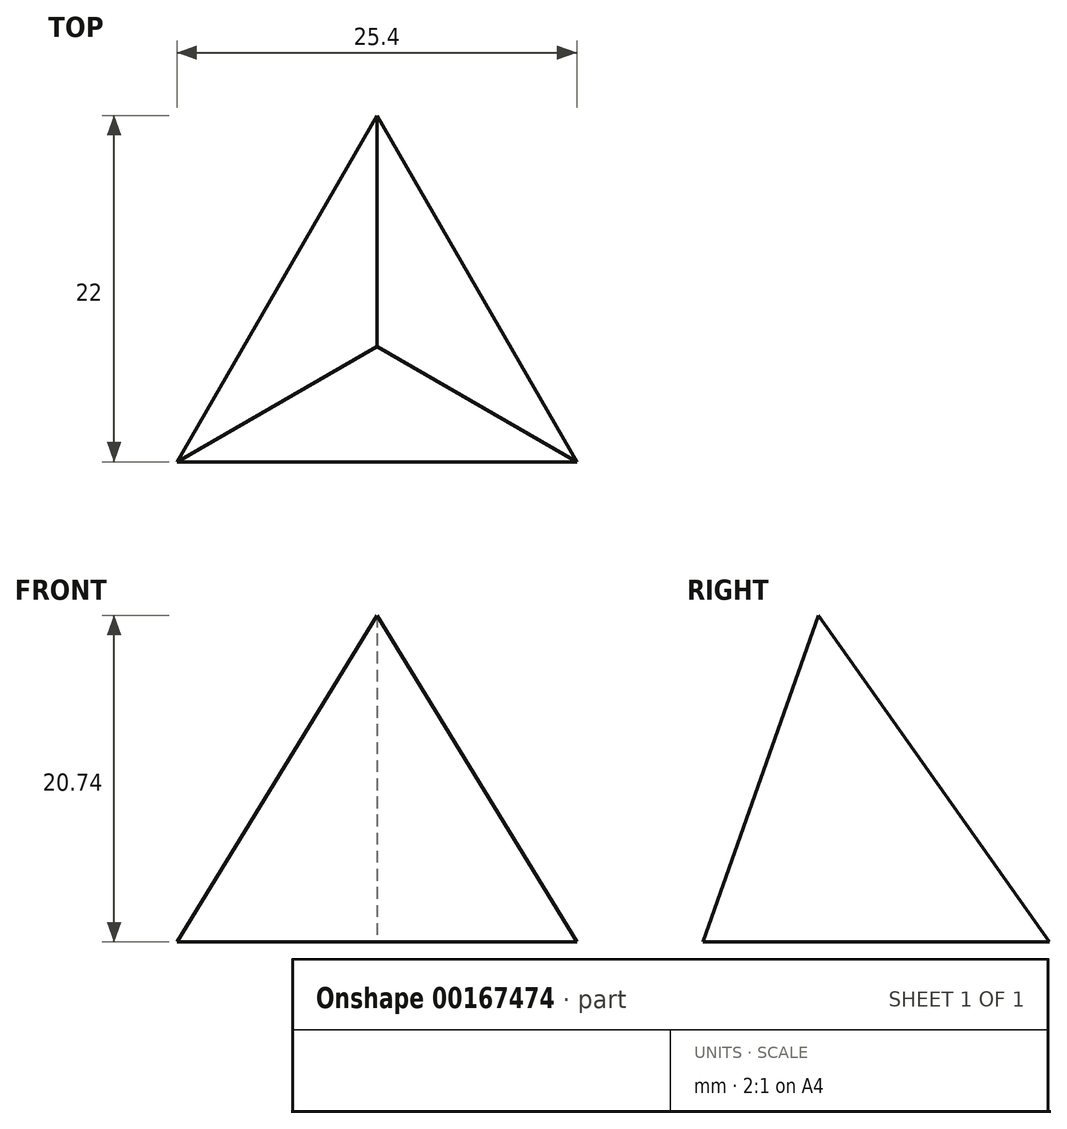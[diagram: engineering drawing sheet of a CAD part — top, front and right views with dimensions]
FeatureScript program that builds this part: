
annotation { "Feature Type Name" : "Feature", "Feature Type Description" : "" }
export const myFeature = defineFeature(function(context is Context, id is Id, definition is map)
    precondition{}
    {
        {
            var Q0;
            Q0=qCreatedBy(makeId("Top.planeOp"),FACE);
            var sketch = newSketch(context, id + "F0", { "sketchPlane" : qUnion([Q0])});
            skLineSegment(sketch, "E0", {"start": v(-12.7, 0) * mm, "end": v(0, 22) * mm});
            skLineSegment(sketch, "E1", {"start": v(0, 22) * mm, "end": v(12.7, 0) * mm});
            skLineSegment(sketch, "E2", {"start": v(12.7, 0) * mm, "end": v(-12.7, 0) * mm});
            skSolve(sketch);
        }
        {
            var Q0;
            Q0 = qSketchRegion(id + "F0", true);
            extrude(context, id + "F1", {"entities" : qUnion([Q0]), "depth" : 26.67 * mm, "hasDraft" : true, "draftAngle" : 90 * degree - atan(2 * (2 ^ 0.5)), "draftPullDirection" : true});
        }
    });
